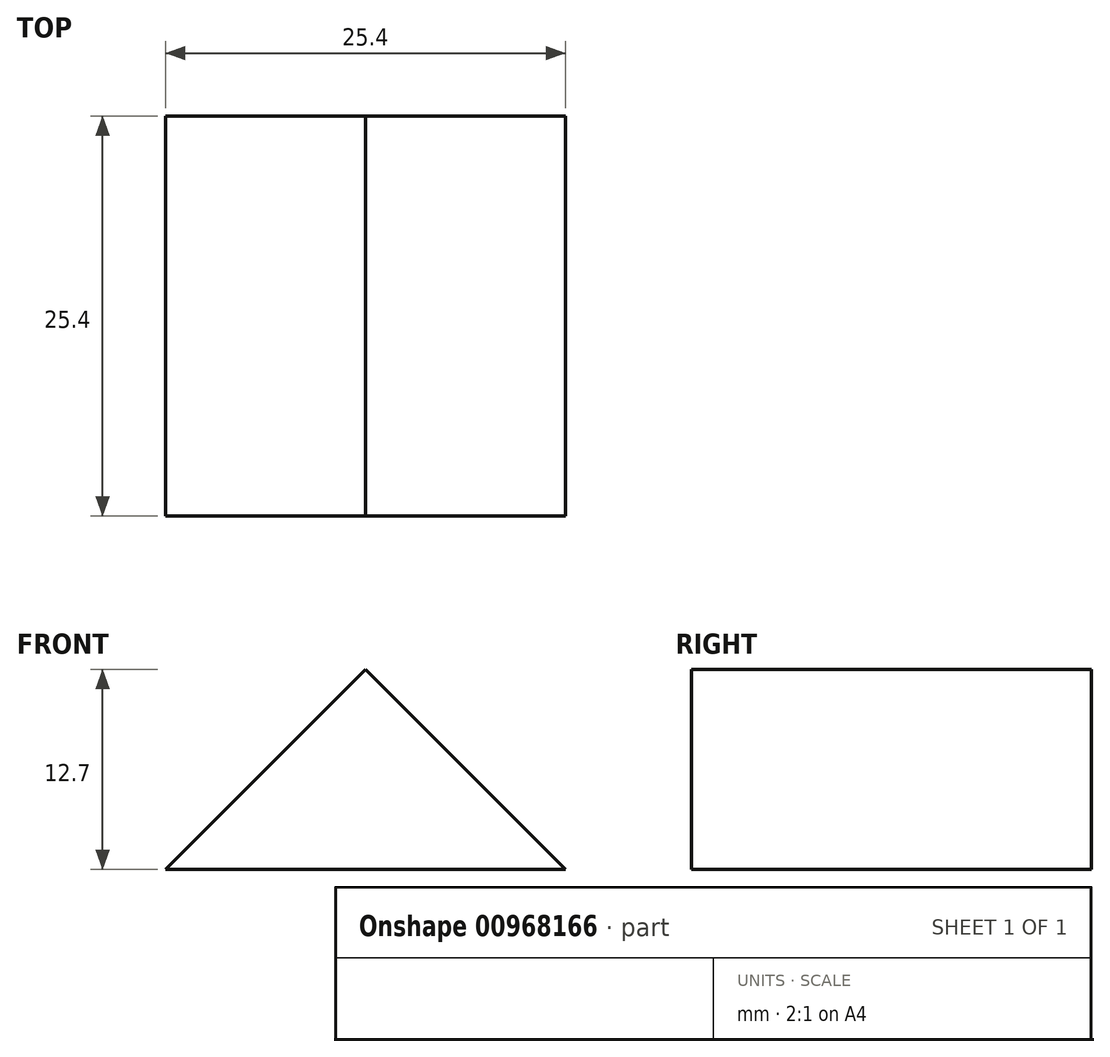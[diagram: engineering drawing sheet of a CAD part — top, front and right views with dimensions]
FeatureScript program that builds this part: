
annotation { "Feature Type Name" : "Feature", "Feature Type Description" : "" }
export const myFeature = defineFeature(function(context is Context, id is Id, definition is map)
    precondition{}
    {
        {
            var Q0;
            Q0=qCreatedBy(makeId("Front.planeOp"),FACE);
            var sketch = newSketch(context, id + "F0", { "sketchPlane" : qUnion([Q0])});
            skLineSegment(sketch, "E0", {"start": v(-8.42, 22.79) * mm, "end": v(-8.42, -2.61) * mm});
            skLineSegment(sketch, "E1", {"start": v(-8.42, -2.61) * mm, "end": v(16.98, -2.61) * mm});
            skLineSegment(sketch, "E2", {"start": v(16.98, -2.61) * mm, "end": v(16.98, 22.79) * mm});
            skLineSegment(sketch, "E3", {"start": v(16.98, 22.79) * mm, "end": v(-8.42, 22.79) * mm});
            skSolve(sketch);
        }
        {
            var Q0;
            Q0 = qSketchRegion(id + "F0", true);
            extrude(context, id + "F1", {"entities" : qUnion([Q0]), "depth" : 25.4 * mm, "offsetDistance" : 25.4 * mm});
        }
        {
            var Q0;
            Q0=makeQuery(id+"F1.opExtrude","CAP_FACE",FACE,{"disambiguationData":[OSD([sQuery(id+"F0.wireOp",EDGE,"E0"),sQuery(id+"F0.wireOp",EDGE,"E1"),sQuery(id+"F0.wireOp",EDGE,"E2"),sQuery(id+"F0.wireOp",EDGE,"E3")])],"isStart":true});
            var sketch = newSketch(context, id + "F2", { "sketchPlane" : qUnion([Q0])});
            skLineSegment(sketch, "E4", {"start": v(-4.28, 10.09) * mm, "end": v(8.42, -2.61) * mm});
            skLineSegment(sketch, "E5", {"start": v(-4.28, 10.09) * mm, "end": v(-16.98, -2.61) * mm});
            skLineSegment(sketch, "E6", {"start": v(8.42, -2.61) * mm, "end": v(8.42, 22.79) * mm});
            skLineSegment(sketch, "E7", {"start": v(8.42, 22.79) * mm, "end": v(-16.98, 22.79) * mm});
            skLineSegment(sketch, "E8", {"start": v(-16.98, 22.79) * mm, "end": v(-16.98, -2.61) * mm});
            skSolve(sketch);
        }
        {
            var Q0;
            Q0 = qSketchRegion(id + "F2", true);
            extrude(context, id + "F3", {"entities" : qUnion([Q0]), "operationType" : NewBodyOperationType.REMOVE, "oppositeDirection" : true, "depth" : 25.4 * mm, "offsetDistance" : 25.4 * mm});
        }
    });
